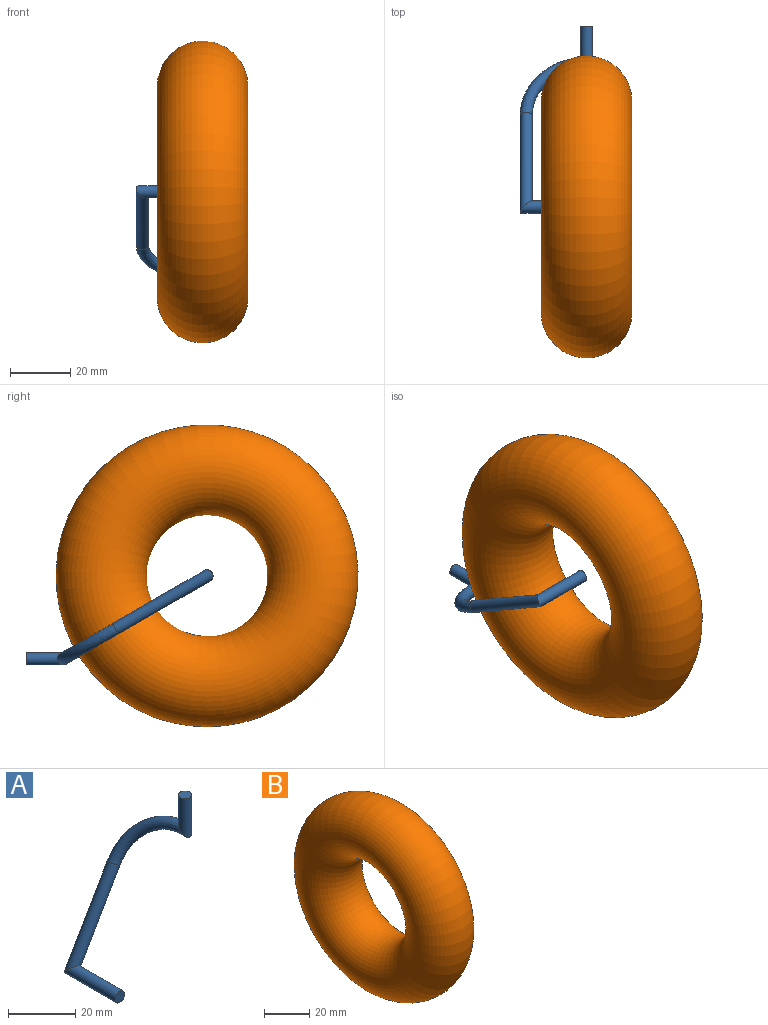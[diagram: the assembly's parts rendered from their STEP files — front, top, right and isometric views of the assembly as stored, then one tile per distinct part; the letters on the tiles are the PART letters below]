
ASSEMBLY  parts=2 mates=1
PART A: 6 faces, bbox 32.2x24x62.7 mm
  f0: plane 4x4mm, normal (0,0,1), area 12.6mm2, adj f2
  f1: plane 4x4mm, normal (0,-1,0), area 12.6mm2, adj f5
  f2: cylinder r=2mm len=14.3mm, axis (0,0,1), area 154.9mm2, adj f0,f4
  f3: cylinder r=2mm len=34.04mm, axis (0.5,0,0.87), area 439.8mm2, adj f4,f5
  f4: bspline ~23.97x20.3mm, area 394.7mm2, adj f2,f3
  f5: cylinder r=2mm len=22mm, axis (0,1,0), area 251.3mm2, adj f1,f3
PART B: 1 faces, bbox 30x108.2x108.2 mm
  f0: torus R=35mm, axis (1,0,0), area 20726.2mm2
PLACE A rot(axis=(-0.58,0.58,0.58),120deg) t=(29.44,22.64,8.46)mm
PLACE B t=(29.44,22.64,8.46)mm
MATE revolute A.f5 <-> B.f0  axis (1,0,0) through (29.44,22.64,8.46)mm
